# Revit family: EKF_EE_РамаШкафаAVTrivia_AVERES
name_source: partatom
category: Электрооборудование
units: mm (PartAtom-declared; Revit-internal decimal feet)

## family parameters
Всегда вертикально = Нет
На основе рабочей плоскости = Да
Общий = Да
При загрузке вырезать с полостями = Нет
Размер круглого соединителя = Использовать диаметр
Тип детали = Силовой щит
Точка расчета площади = Нет

## types (3) — shared parameters
ADSK_Единица измерения = шт.
ADSK_Завод-изготовитель = EKF
ADSK_Количество = 1
ADSK_Марка = Рама шкафа AV Trivia
ADSK_Материал = RAL 7035_Сталь
ADSK_Обозначение = Рама шкафа AV Trivia
ADSK_Размер_Высота = 2010 мм
ADSK_Размер_Ширина = 43 мм
Изготовитель = EKF
Серия номенклатуры = Averes
Степень защиты IP = -
ТВ = EKF_2_TRIVIA_AVERES
Тип установки = -
zero-valued in all types: ADSK_Масса, Отметка по умолчанию

## per-type parameters (varying)
| type | ADSK_Код изделия | ADSK_Размер_Глубина | Тип |
| Рама шкафа AV Trivia В2000 Г400 (комплект из 2-х) EKF AVERES | F2D400 | 410 мм | 405 мм |
| Рама шкафа AV Trivia В2000 Г600 (комплект из 2-х) EKF AVERES | F2D600 | 610 мм | 406 мм |
| Рама шкафа AV Trivia В2000 Г800 (комплект из 2-х) EKF AVERES | F2D800 | 810 мм | 407 мм |

note: column(s) folded — value = type name in every type: ADSK_Наименование
